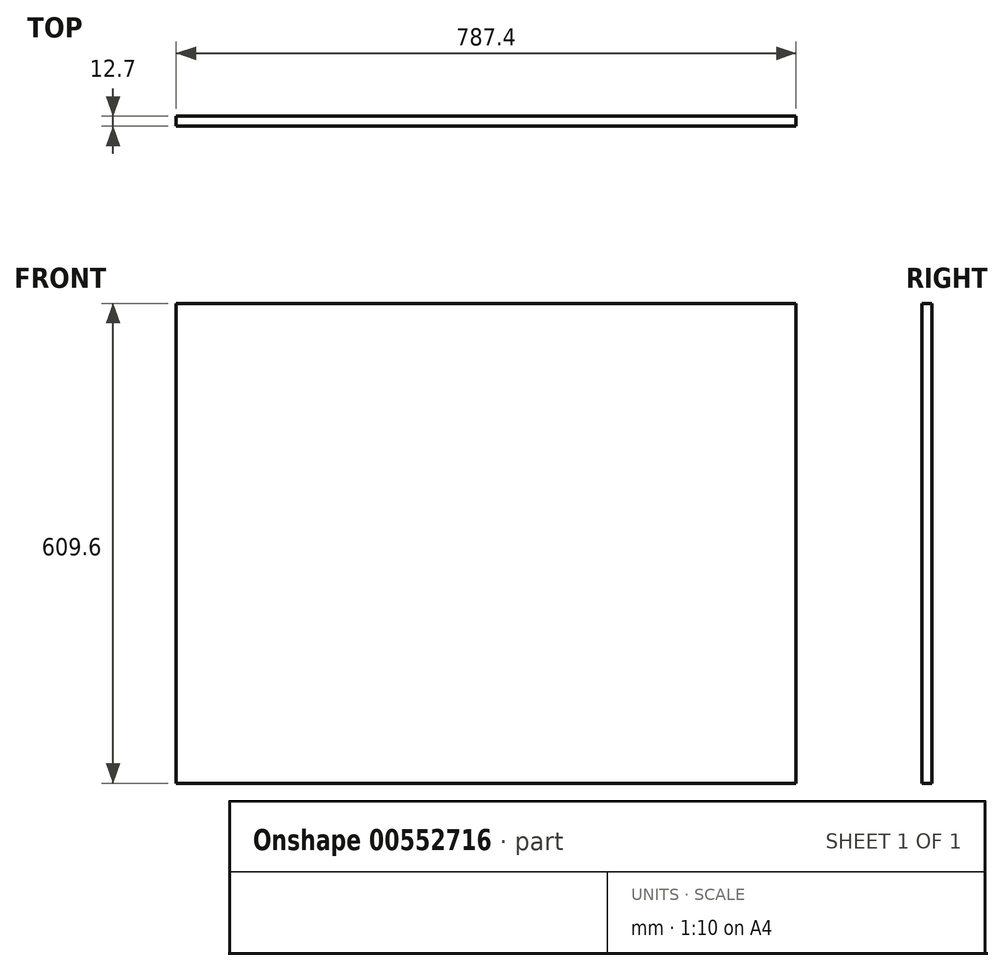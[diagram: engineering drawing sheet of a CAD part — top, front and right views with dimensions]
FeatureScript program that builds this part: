
annotation { "Feature Type Name" : "Feature", "Feature Type Description" : "" }
export const myFeature = defineFeature(function(context is Context, id is Id, definition is map)
    precondition{}
    {
        {
            var Q0;
            Q0=qCreatedBy(makeId("Front.planeOp"),FACE);
            var sketch = newSketch(context, id + "F0", { "sketchPlane" : qUnion([Q0])});
            skLineSegment(sketch, "E0.bottom", {"start": v(393.7, -304.8) * mm, "end": v(-393.7, -304.8) * mm});
            skLineSegment(sketch, "E0.top", {"start": v(393.7, 304.8) * mm, "end": v(-393.7, 304.8) * mm});
            skLineSegment(sketch, "E0.left", {"start": v(393.7, -304.8) * mm, "end": v(393.7, 304.8) * mm});
            skLineSegment(sketch, "E0.right", {"start": v(-393.7, -304.8) * mm, "end": v(-393.7, 304.8) * mm});
            skPoint(sketch, "E0.middle", {"position": v(0, 0) * mm});
            skSolve(sketch);
        }
        {
            var Q0;
            Q0=makeQuery(id+"F0.imprint","IMPRINT",FACE,{"disambiguationData":[TD([[makeQuery(id+"F0.imprint","IMPRINT",EDGE,{"derivedFrom":sQuery(id+"F0.wireOp",EDGE,"E0.bottom")}),-1.0]])]});
            extrude(context, id + "F1", {"entities" : qUnion([Q0]), "endBound" : BoundingType.SYMMETRIC, "oppositeDirection" : true, "depth" : 12.7 * mm, "offsetDistance" : 25.4 * mm});
        }
    });
